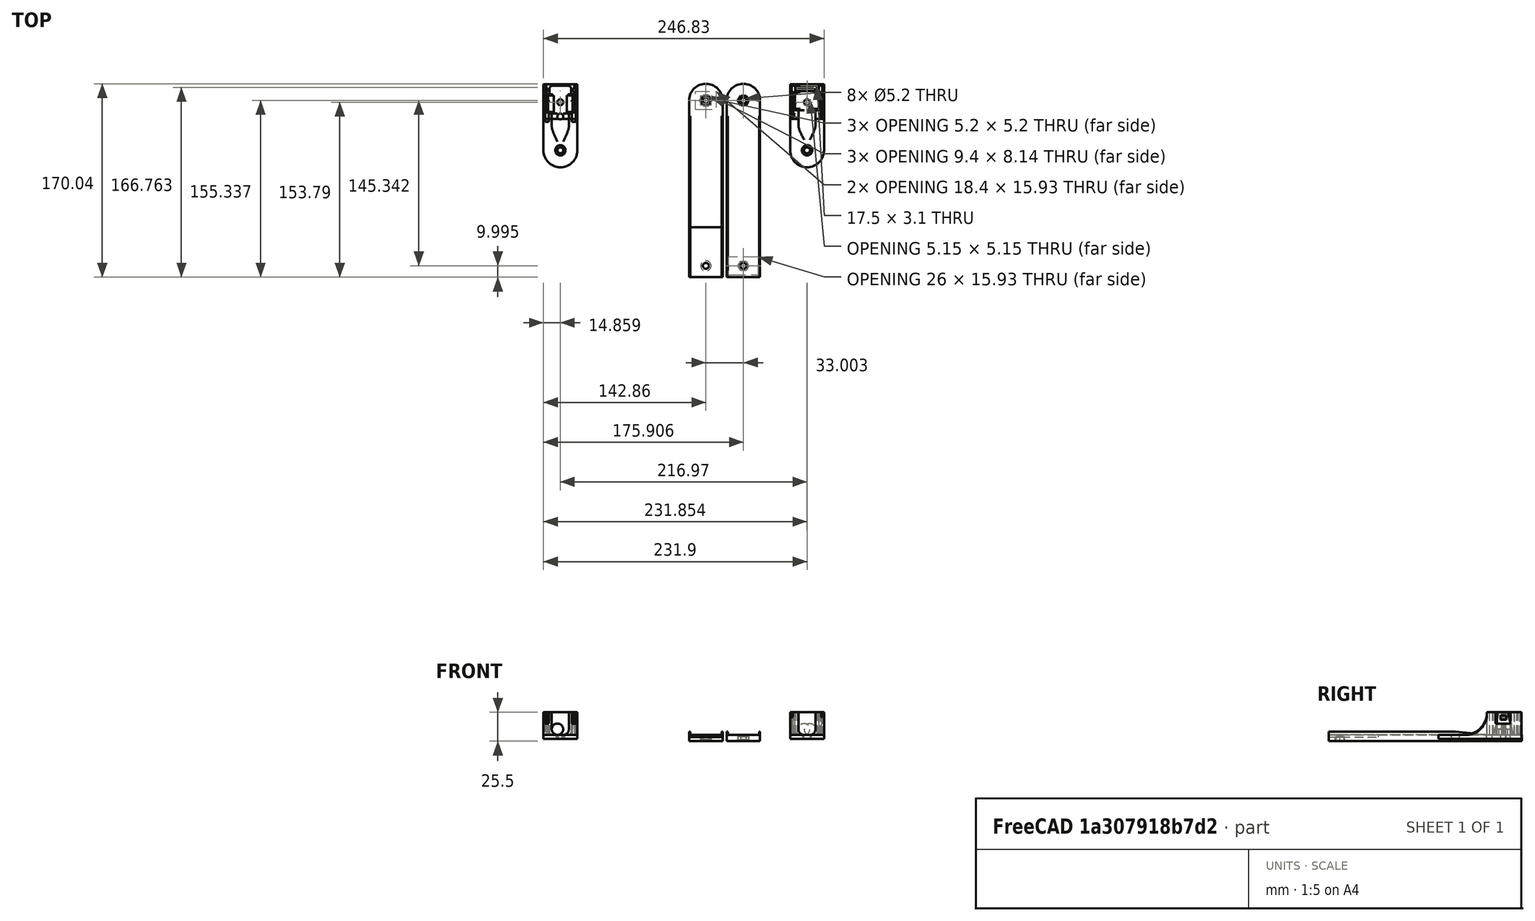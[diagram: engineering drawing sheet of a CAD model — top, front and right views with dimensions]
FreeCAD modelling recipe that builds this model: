
FCSTD DOCUMENT  (FreeCAD 0.18.4R)
Label: tmp2
License: All rights reserved
LicenseURL: http://en.wikipedia.org/wiki/All_rights_reserved
objects: Part::Part2DObjectPython×25, Part::FeaturePython×15, Part::MultiFuse×14, Part::Cut×8, Part::Feature×6, Part::Extrusion×5, App::DocumentObjectGroup×3
note: 73 computed .brp shape members not serialized (recipe doc carries the construction recipe); baked Part::Feature solids carry a one-line shape summary decoded from their .brp

FEATURE [Part::MultiFuse] Fusion005002002014004003003002009002010004002003006003008008004007002004006006004008003005011012015
FEATURE [Part::MultiFuse] Fusion005002002014004003003002009002010004002003006003008008004007002004006006004008003005011012011
FEATURE [Part::FeaturePython] Slice008_child1  label="Slice008.1"  # WARN: FeaturePython — macro-defined, semantics opaque (R4)
  FilterType = 1
  Invert = false
  OverrideMaxVal = 0
  Placement = pos=(-1.76886,5.5e-14,-5e-15) rot=(0,0,1;0rad)
  WindowFrom = 80
  WindowTo = 100
  items = 1
FEATURE [Part::FeaturePython] Slice007_child2  label="Slice007.2"  # WARN: FeaturePython — macro-defined, semantics opaque (R4)
  FilterType = 1
  Invert = false
  OverrideMaxVal = 0
  Placement = pos=(1.74591,-2e-15,4e-15) rot=(0,0,1;0rad)
  WindowFrom = 80
  WindowTo = 100
  items = 2
FEATURE [Part::Cut] Cut004006005004002008019023005025020
  Placement = pos=(21.0148,0,-4.62053e-09) rot=(0,0,1;0rad)
FEATURE [Part::Cut] Cut004006005004002008019023005025017
FEATURE [Part::Cut] Cut004006005004002008019023005025016
FEATURE [Part::FeaturePython] Slice009_child1  label="Slice009.1"  # WARN: FeaturePython — macro-defined, semantics opaque (R4)
  FilterType = 1
  Invert = false
  OverrideMaxVal = 0
  WindowFrom = 80
  WindowTo = 100
  items = 1
FEATURE [Part::Cut] Cut004006005004002008019023005025019
FEATURE [Part::FeaturePython] Slice009_child0  label="Slice009.0"  # WARN: FeaturePython — macro-defined, semantics opaque (R4)
  FilterType = 1
  Invert = false
  OverrideMaxVal = 0
  WindowFrom = 80
  WindowTo = 100
  items = 0
FEATURE [Part::MultiFuse] Fusion
  Shapes = -> [Fusion005002002014004003003002009002010004002003006003008008004007002004006006004008003005011012015,Fusion005002002014004003003002009002010004002003006003008008004007002004006006004008003005011012011]
FEATURE [Part::MultiFuse] Fusion005002002014004003003002009002010004002003006003008008004007002004006006004008003005011012016
  Shapes = -> [Fusion,Slice007_child2]
FEATURE [Part::MultiFuse] Fusion005002002014004003003002009002010004002003006003008008004007002004006006004008003005011012017
  Shapes = -> [Cut004006005004002008019023005025019,Cut004006005004002008019023005025017]
FEATURE [Part::MultiFuse] Fusion005002002014004003003002009002010004002003006003008008004007002004006006004008003005011012018
  Shapes = -> [Fusion005002002014004003003002009002010004002003006003008008004007002004006006004008003005011012016,Fusion005002002014004003003002009002010004002003006003008008004007002004006006004008003005011012017]
FEATURE [Part::MultiFuse] Fusion005002002014004003003002009002010004002003006003008008004007002004006006004008003005011012019
  Shapes = -> [Fusion005002002014004003003002009002010004002003006003008008004007002004006006004008003005011012018,Slice008_child1,Slice009_child1,Slice009_child0,Cut004006005004002008019023005025016]
FEATURE [Part::MultiFuse] Fusion005002002014004003003002009002010004002003006003008008004007002004006006004008003005011012020
  Shapes = -> [Fusion005002002014004003003002009002010004002003006003008008004007002004006006004008003005011012019,Cut004006005004002008019023005025020]
FEATURE [Part::Part2DObjectPython] Rectangle  # Draft 2D object (typed FeaturePython)
  ChamferSize = 0
  Columns = 1
  FilletRadius = 0
  Height = 0.5
  Length = 1.4
  MakeFace = true
  Placement = pos=(-778.23,-7.22458,16.3661) rot=(0,0,-1;1.5708rad)
  Rows = 1
  Support = -> [Fusion005002002014004003003002009002010004002003006003008008004007002004006006004008003005011012020]
FEATURE [Part::Extrusion] Extrusion
  Base = -> Rectangle
  Dir = (-1.633e-13,8.25e-14,-15)
  DirMode = 0
  FaceMakerClass = Part::FaceMakerBullseye
  LengthFwd = 0
  LengthRev = 0
  Solid = true
  Symmetric = false
FEATURE [Part::Feature] Face
  Placement = pos=(-778.23,-7.22458,1.36605) rot=(0,0,-1;1.5708rad)
  shape: bbox 0.5 x 1.4 x 2.759e-06 mm, 1 faces, 0 solids (baked)
FEATURE [Part::Extrusion] Extrusion001
  Base = -> Face
  Dir = (-5.44e-14,2.75e-14,-5)
  DirMode = 0
  FaceMakerClass = Part::FaceMakerBullseye
  LengthFwd = 0
  LengthRev = 0
  Solid = true
  Symmetric = false
FEATURE [Part::MultiFuse] Fusion005002002014004003003002009002010004002003006003008008004007002004006006004008003005011012021
  Shapes = -> [Fusion005002002014004003003002009002010004002003006003008008004007002004006006004008003005011012020,Extrusion]
FEATURE [Part::MultiFuse] Fusion005002002014004003003002009002010004002003006003008008004007002004006006004008003005011012022
  Shapes = -> [Extrusion001,Fusion005002002014004003003002009002010004002003006003008008004007002004006006004008003005011012021]
FEATURE [Part::Part2DObjectPython] Circle  # Draft 2D object (typed FeaturePython)
  FirstAngle = 0
  LastAngle = 0
  MakeFace = true
  Placement = pos=(-767.462,-21.4707,-3.63395) rot=(0,0,1;0rad)
  Radius = 2.59507
FEATURE [Part::Extrusion] Extrusion002
  Base = -> Circle
  Dir = (1.213e-13,-2.236e-13,-100.251)
  DirMode = 0
  FaceMakerClass = Part::FaceMakerBullseye
  LengthFwd = 0
  LengthRev = 0
  Placement = pos=(-1.14e-13,1.1e-13,50.1257) rot=(0,0,1;0rad)
  Solid = true
  Symmetric = false
FEATURE [Part::Cut] Cut
  Base = -> Fusion005002002014004003003002009002010004002003006003008008004007002004006006004008003005011012022
  Tool = -> Extrusion002
FEATURE [Part::Part2DObjectPython] Rectangle001  # Draft 2D object (typed FeaturePython)
  ChamferSize = 0
  Columns = 1
  FilletRadius = 0
  Height = 100
  Length = 100
  MakeFace = true
  Placement = pos=(-824.962,-23.4762,66.3661) rot=(-1,0,0;1.5708rad)
  Rows = 1
  Support = -> [Cut]
FEATURE [Part::FeaturePython] Slice  # WARN: FeaturePython — macro-defined, semantics opaque (R4)
  Base = -> Cut
  Mode = 1
  Tolerance = 0
  Tools = -> [Rectangle001]
FEATURE [Part::FeaturePython] Slice_child0002  label="Slice.002"  # WARN: FeaturePython — macro-defined, semantics opaque (R4)
  Base = -> Slice
  FilterType = 1
  Invert = false
  OverrideMaxVal = 0
  WindowFrom = 80
  WindowTo = 100
  items = 0
FEATURE [Part::FeaturePython] Slice_child1  label="Slice.1"  # WARN: FeaturePython — macro-defined, semantics opaque (R4)
  Base = -> Slice
  FilterType = 1
  Invert = false
  OverrideMaxVal = 0
  WindowFrom = 80
  WindowTo = 100
  items = 1
FEATURE [App::DocumentObjectGroup] GrExplode_Slice  label="Exploded Slice"
  Group = -> [Slice_child0002,Slice_child1]
FEATURE [Part::Cut] Cut001
  Base = -> Cut
  Placement = pos=(-0.0703521,-2.27e-13,8.2e-14) rot=(0,0,1;0rad)
  Tool = -> Extrusion001
FEATURE [Part::Part2DObjectPython] Line001  # Draft 2D object (typed FeaturePython)
  ChamferSize = 0
  Closed = false
  End = (-719.991,5.52378,14.8661)
  FilletRadius = 0
  Length = 1.64151
  MakeFace = true
  Placement = pos=(-719.324,5.52378,16.3661) rot=(0,0,1;0rad)
  Points = (2) [(0,0,0),(-0.666752,0,-1.5)]
  Start = (-719.324,5.52378,16.3661)
  Subdivisions = 0
FEATURE [Part::Part2DObjectPython] Line  # Draft 2D object (typed FeaturePython)
  ChamferSize = 0
  Closed = false
  End = (-719.991,5.52378,14.8661)
  FilletRadius = 0
  Length = 12.1
  MakeFace = true
  Placement = pos=(-719.991,-6.57622,14.8661) rot=(0,0,1;0rad)
  Points = (2) [(0,0,0),(0,12.1,0)]
  Start = (-719.991,-6.57622,14.8661)
  Subdivisions = 0
FEATURE [Part::Part2DObjectPython] Line003  # Draft 2D object (typed FeaturePython)
  ChamferSize = 0
  Closed = false
  End = (-779.702,-23.4762,13.8661)
  FilletRadius = 0
  Length = 3.15957
  MakeFace = true
  Placement = pos=(-777.77,-23.4762,16.3661) rot=(0,0.707107,0.707107;3.14159rad)
  Points = (2) [(0,0,0),(1.93206,-2.5,-8.88178e-14)]
  Start = (-777.77,-23.4762,16.3661)
  Subdivisions = 0
  Support = -> [Slice_child1]
FEATURE [Part::Part2DObjectPython] Line004  # Draft 2D object (typed FeaturePython)
  ChamferSize = 0
  Closed = false
  End = (-779.702,-23.4762,13.8661)
  FilletRadius = 0
  Length = 12.1033
  MakeFace = true
  Placement = pos=(-779.702,-11.3746,13.6661) rot=(0,0.707107,0.707107;3.14159rad)
  Points = (2) [(0,0,0),(-3.41061e-13,0.2,-12.1016)]
  Start = (-779.702,-11.3746,13.6661)
  Subdivisions = 0
FEATURE [Part::Part2DObjectPython] Line006  # Draft 2D object (typed FeaturePython)
  ChamferSize = 0
  Closed = false
  End = (-780.327,5.52378,13.6661)
  FilletRadius = 0
  Length = 2.77139
  MakeFace = true
  Placement = pos=(-780.952,5.52378,16.3661) rot=(0,0,1;0rad)
  Points = (2) [(0,0,0),(0.625,-2.66454e-15,-2.7)]
  Start = (-780.952,5.52378,16.3661)
  Subdivisions = 0
FEATURE [Part::Part2DObjectPython] Line007  # Draft 2D object (typed FeaturePython)
  ChamferSize = 0
  Closed = false
  End = (-780.327,-6.37457,13.6661)
  FilletRadius = 0
  Length = 11.8984
  MakeFace = true
  Placement = pos=(-780.327,5.52378,13.6661) rot=(0,0,1;0rad)
  Points = (2) [(0,0,0),(0,-11.8984,-1.77636e-15)]
  Start = (-780.327,5.52378,13.6661)
  Subdivisions = 0
FEATURE [Part::Part2DObjectPython] Line009  # Draft 2D object (typed FeaturePython)
  ChamferSize = 0
  Closed = false
  End = (-719.991,-23.4762,14.8661)
  FilletRadius = 0
  Length = 1.5
  MakeFace = true
  Placement = pos=(-719.991,-23.4762,16.3661) rot=(0,0,1;0rad)
  Points = (2) [(0,0,0),(-2.27374e-13,-3.55271e-15,-1.5)]
  Start = (-719.991,-23.4762,16.3661)
  Subdivisions = 0
FEATURE [Part::Part2DObjectPython] Line011  # Draft 2D object (typed FeaturePython)
  ChamferSize = 0
  Closed = false
  End = (-720.991,-11.5762,14.8661)
  FilletRadius = 0
  Length = 5
  MakeFace = true
  Placement = pos=(-720.991,-6.57622,14.8661) rot=(0,0,1;0rad)
  Points = (2) [(0,0,0),(0,-5,3.55271e-14)]
  Start = (-720.991,-6.57622,14.8661)
  Subdivisions = 0
FEATURE [Part::Feature] Face001
  Placement = pos=(-662.622,-18.8412,29.4029) rot=(0,0.707107,0.707107;3.14159rad)
  shape: bbox 2 x 7.594e-07 x 4 mm, 1 faces, 0 solids (baked)
FEATURE [Part::Part2DObjectPython] Line012  # Draft 2D object (typed FeaturePython)
  ChamferSize = 0
  Closed = false
  End = (-719.991,-23.4762,14.8661)
  FilletRadius = 0
  Length = 11.9
  MakeFace = true
  Placement = pos=(-719.991,-11.5762,14.8661) rot=(0,0,1;0rad)
  Points = (2) [(0,0,0),(0,-11.9,1.24345e-14)]
  Start = (-719.991,-11.5762,14.8661)
  Subdivisions = 0
FEATURE [Part::Part2DObjectPython] Rectangle002  # Draft 2D object (typed FeaturePython)
  ChamferSize = 0
  Columns = 1
  FilletRadius = 0
  Height = 12.3395
  Length = 25.6813
  MakeFace = true
  Placement = pos=(-720.26,-15.3132,-3.63395) rot=(0,0,1;0rad)
  Rows = 1
  Support = -> [Cut001]
FEATURE [Part::FeaturePython] Slice001  # WARN: FeaturePython — macro-defined, semantics opaque (R4)
  Base = -> Cut001
  Mode = 1
  Tolerance = 0
  Tools = -> [Rectangle002]
FEATURE [App::DocumentObjectGroup] GrExplode_Slice001  label="Exploded Slice001"
FEATURE [Part::FeaturePython] Slice001_child0  label="Slice001.0"  # WARN: FeaturePython — macro-defined, semantics opaque (R4)
  Base = -> Slice001
  FilterType = 1
  Invert = false
  OverrideMaxVal = 0
  WindowFrom = 80
  WindowTo = 100
  items = 0
FEATURE [Part::Part2DObjectPython] Rectangle003  # Draft 2D object (typed FeaturePython)
  ChamferSize = 0
  Columns = 1
  FilletRadius = 0
  Height = 15.9501
  Length = 26.1599
  MakeFace = true
  Placement = pos=(-780.589,-18.3063,-3.63395) rot=(0,0,1;0rad)
  Rows = 1
FEATURE [Part::FeaturePython] Slice002  # WARN: FeaturePython — macro-defined, semantics opaque (R4)
  Base = -> Slice_child0002
  Mode = 1
  Tolerance = 0
  Tools = -> [Rectangle003]
FEATURE [Part::FeaturePython] Slice002_child0  label="Slice002.0"  # WARN: FeaturePython — macro-defined, semantics opaque (R4)
  Base = -> Slice002
  FilterType = 1
  Invert = false
  OverrideMaxVal = 0
  Placement = pos=(29.2881,-0.491384,-5.6e-14) rot=(0,0,1;0rad)
  WindowFrom = 80
  WindowTo = 100
  items = 0
FEATURE [Part::FeaturePython] Slice002_child1  label="Slice002.1"  # WARN: FeaturePython — macro-defined, semantics opaque (R4)
  Base = -> Slice002
  FilterType = 1
  Invert = false
  OverrideMaxVal = 0
  WindowFrom = 80
  WindowTo = 100
  items = 1
FEATURE [Part::FeaturePython] Slice002_child2  label="Slice002.2"  # WARN: FeaturePython — macro-defined, semantics opaque (R4)
  Base = -> Slice002
  FilterType = 1
  Invert = false
  OverrideMaxVal = 0
  Placement = pos=(29.2881,-0.491384,-5.6e-14) rot=(0,0,1;0rad)
  WindowFrom = 80
  WindowTo = 100
  items = 2
FEATURE [Part::FeaturePython] Slice002_child003  label="Slice002.003"  # WARN: FeaturePython — macro-defined, semantics opaque (R4)
  Base = -> Slice002
  FilterType = 1
  Invert = false
  OverrideMaxVal = 0
  WindowFrom = 80
  WindowTo = 100
  items = 0
FEATURE [Part::FeaturePython] Slice002_child004  label="Slice002.004"  # WARN: FeaturePython — macro-defined, semantics opaque (R4)
  Base = -> Slice002
  FilterType = 1
  Invert = false
  OverrideMaxVal = 0
  WindowFrom = 80
  WindowTo = 100
  items = 2
FEATURE [Part::MultiFuse] Fusion005002002014004003003002009002010004002003006003008008004007002004006006004008003005011012023
  Placement = pos=(-1445.64,-17.9925,-5.19e-13) rot=(0,0,1;3.14159rad)
  Shapes = -> [Slice002_child2,Slice002_child0]
FEATURE [Part::Part2DObjectPython] Line017  # Draft 2D object (typed FeaturePython)
  ChamferSize = 0
  Closed = false
  End = (-725.927,-8.41596,16.3661)
  FilletRadius = 0
  Length = 24.4871
  MakeFace = true
  Placement = pos=(-750.414,-8.41596,16.3661) rot=(0,0,1;0rad)
  Points = (2) [(0,0,0),(24.4871,-1.4353e-12,-7.10543e-15)]
  Start = (-750.414,-8.41596,16.3661)
  Subdivisions = 0
FEATURE [Part::Part2DObjectPython] Line018  # Draft 2D object (typed FeaturePython)
  ChamferSize = 0
  Closed = false
  End = (-670.52,-33.508,-7.13395)
  FilletRadius = 0
  Length = 97
  MakeFace = true
  Placement = pos=(-767.52,-33.508,-7.13395) rot=(1,0,0;3.14159rad)
  Points = (2) [(0,0,0),(97,7.10543e-15,0)]
  Start = (-767.52,-33.508,-7.13395)
  Subdivisions = 0
  Support = -> [Slice_child1]
FEATURE [Part::Part2DObjectPython] Line019  # Draft 2D object (typed FeaturePython)
  ChamferSize = 0
  Closed = false
  End = (-719.991,-11.5762,-33.2339)
  FilletRadius = 0
  Length = 48.1
  MakeFace = true
  Placement = pos=(-719.991,-11.5762,14.8661) rot=(0,0.707107,-0.707107;3.14159rad)
  Points = (2) [(0,0,0),(1.13687e-13,48.1,-7.10543e-15)]
  Start = (-719.991,-11.5762,14.8661)
  Subdivisions = 0
  Support = -> [Fusion005002002014004003003002009002010004002003006003008008004007002004006006004008003005011012023]
FEATURE [Part::Part2DObjectPython] Line020  # Draft 2D object (typed FeaturePython)
  ChamferSize = 0
  Closed = false
  End = (-719.991,-6.57622,-33.2339)
  FilletRadius = 0
  Length = 48.1
  MakeFace = true
  Placement = pos=(-719.991,-6.57622,14.8661) rot=(0,0.707107,-0.707107;3.14159rad)
  Points = (2) [(0,0,0),(1.13687e-13,48.1,-4.44089e-15)]
  Start = (-719.991,-6.57622,14.8661)
  Subdivisions = 0
FEATURE [Part::Part2DObjectPython] Line021  # Draft 2D object (typed FeaturePython)
  ChamferSize = 0
  Closed = false
  End = (-749.702,-11.3746,13.6661)
  FilletRadius = 0
  Length = 31.2499
  MakeFace = true
  Placement = pos=(-780.952,-11.3746,13.6661) rot=(0,0,1;3.14159rad)
  Points = (2) [(0,0,0),(-31.2499,1.93623e-13,-1.59872e-14)]
  Start = (-780.952,-11.3746,13.6661)
  Subdivisions = 0
  Support = -> [Slice002_child003]
FEATURE [Part::Part2DObjectPython] Line022  # Draft 2D object (typed FeaturePython)
  ChamferSize = 0
  Closed = false
  End = (-749.327,-6.37457,13.6661)
  FilletRadius = 0
  Length = 31.625
  MakeFace = true
  Placement = pos=(-780.952,-6.37457,13.6661) rot=(0,0,1;3.14159rad)
  Points = (2) [(0,0,0),(-31.625,2.03393e-13,-2.13163e-14)]
  Start = (-780.952,-6.37457,13.6661)
  Subdivisions = 0
FEATURE [Part::Feature] Face002
  shape: bbox 1.241 x 1.943e-06 x 3.8 mm, 1 faces, 0 solids (baked)
FEATURE [Part::Extrusion] Extrusion003
  Base = -> Face002
  Dir = (-3.05e-14,-0.500548,0)
  DirMode = 0
  FaceMakerClass = Part::FaceMakerBullseye
  LengthFwd = 0
  LengthRev = 0
  Solid = true
  Symmetric = false
FEATURE [Part::Cut] Cut004006005004002008019023005025021
  Base = -> Slice002_child004
  Tool = -> Extrusion003
FEATURE [Part::Part2DObjectPython] Line023  # Draft 2D object (typed FeaturePython)
  ChamferSize = 0
  Closed = false
  End = (-720.335,-11.127,13.6661)
  FilletRadius = 0
  Length = 5
  MakeFace = true
  Placement = pos=(-720.335,-6.12704,13.6661) rot=(0,0,1;0rad)
  Points = (2) [(0,0,0),(-4.54747e-13,-5,7.10543e-15)]
  Start = (-720.335,-6.12704,13.6661)
  Subdivisions = 0
  Support = -> [Fusion005002002014004003003002009002010004002003006003008008004007002004006006004008003005011012023]
FEATURE [Part::Part2DObjectPython] Line024  # Draft 2D object (typed FeaturePython)
  ChamferSize = 0
  Closed = false
  End = (-720.956,-11.127,13.6661)
  FilletRadius = 0
  Length = 0.620611
  MakeFace = true
  Placement = pos=(-720.335,-11.127,13.6661) rot=(0,0,1;0rad)
  Points = (2) [(0,0,0),(-0.620611,-7.10543e-15,-5.32907e-15)]
  Start = (-720.335,-11.127,13.6661)
  Subdivisions = 0
FEATURE [Part::Feature] Face005
  Placement = pos=(-1474.93,-17.5011,-6e-13) rot=(0,0,1;3.14159rad)
  shape: bbox 1.241 x 1.943e-06 x 3.8 mm, 1 faces, 0 solids (baked)
FEATURE [Part::Extrusion] Extrusion004
  Base = -> Face005
  Dir = (3.06e-14,0.5,7e-16)
  DirMode = 0
  FaceMakerClass = Part::FaceMakerBullseye
  LengthFwd = 0
  LengthRev = 0
  Solid = true
  Symmetric = false
FEATURE [Part::Cut] Cut004006005004002008019023005025022
  Base = -> Fusion005002002014004003003002009002010004002003006003008008004007002004006006004008003005011012023
  Placement = pos=(0,-0.449178,0) rot=(0,0,1;0rad)
  Tool = -> Extrusion004
FEATURE [Part::Part2DObjectPython] Line025  # Draft 2D object (typed FeaturePython)
  ChamferSize = 0
  Closed = false
  End = (-692.268,-11.127,13.6661)
  FilletRadius = 0
  Length = 28.6875
  MakeFace = true
  Placement = pos=(-720.956,-11.127,13.6661) rot=(0,0,1;0rad)
  Points = (2) [(0,0,0),(28.6875,-3.30402e-13,-3.37508e-14)]
  Start = (-720.956,-11.127,13.6661)
  Subdivisions = 0
FEATURE [Part::Part2DObjectPython] Line026  # Draft 2D object (typed FeaturePython)
  ChamferSize = 0
  Closed = false
  End = (-719.991,-6.57622,13.6661)
  FilletRadius = 0
  Length = 1.064
  MakeFace = true
  Placement = pos=(-720.956,-6.12704,13.6661) rot=(0,0,1;0rad)
  Points = (2) [(0,0,0),(0.964534,-0.449178,0)]
  Start = (-720.956,-6.12704,13.6661)
  Subdivisions = 0
FEATURE [Part::Part2DObjectPython] Line027  # Draft 2D object (typed FeaturePython)
  ChamferSize = 0
  Closed = false
  End = (-719.991,-6.12704,13.6661)
  FilletRadius = 0
  Length = 0.449178
  MakeFace = true
  Placement = pos=(-719.991,-6.57622,13.6661) rot=(0,0,1;0rad)
  Points = (2) [(0,0,0),(0,0.449178,-7.10543e-15)]
  Start = (-719.991,-6.57622,13.6661)
  Subdivisions = 0
FEATURE [Part::MultiFuse] Fusion005002002014004003003002009002010004002003006003008008004007002004006006004008003005011012024
  Placement = pos=(157,-7.1e-15,-3.11e-14) rot=(0,0,1;0rad)
  Shapes = -> [Slice001_child0,Cut004006005004002008019023005025022]
FEATURE [App::DocumentObjectGroup] GrExplode_Slice002  label="Exploded Slice002"
  Group = -> [Slice002_child1,Fusion005002002014004003003002009002010004002003006003008008004007002004006006004008003005011012024]
FEATURE [Part::MultiFuse] Fusion005002002014004003003002009002010004002003006003008008004007002004003
  Placement = pos=(-677.592,-2.54468,-4) rot=(0,0,1;0rad)
FEATURE [Part::MultiFuse] Fusion005002002014004003003002009002010004002003006003008008004007002004006006004008003005011006
  Placement = pos=(-82.9949,0,-5e-15) rot=(0,0,1;0rad)
FEATURE [Part::Feature] Fusion005002002014004003003002009002010004002003006003008008004007002004003001  label="Fusion005002002014004003003002009002010004002003006003008008004007002004006006004008003005011012025"
  shape: bbox 29.42 x 170 x 8.5 mm, 24 faces (baked)
FEATURE [Part::Feature] Fusion005002002014004003003002009002010004002003006003008008004007002004006006004008003005011006001  label="Fusion005002002014004003003002009002010004002003006003008008004007002004006006004008003005011012026"
  shape: bbox 29.42 x 170 x 8.5 mm, 29 faces (baked)
